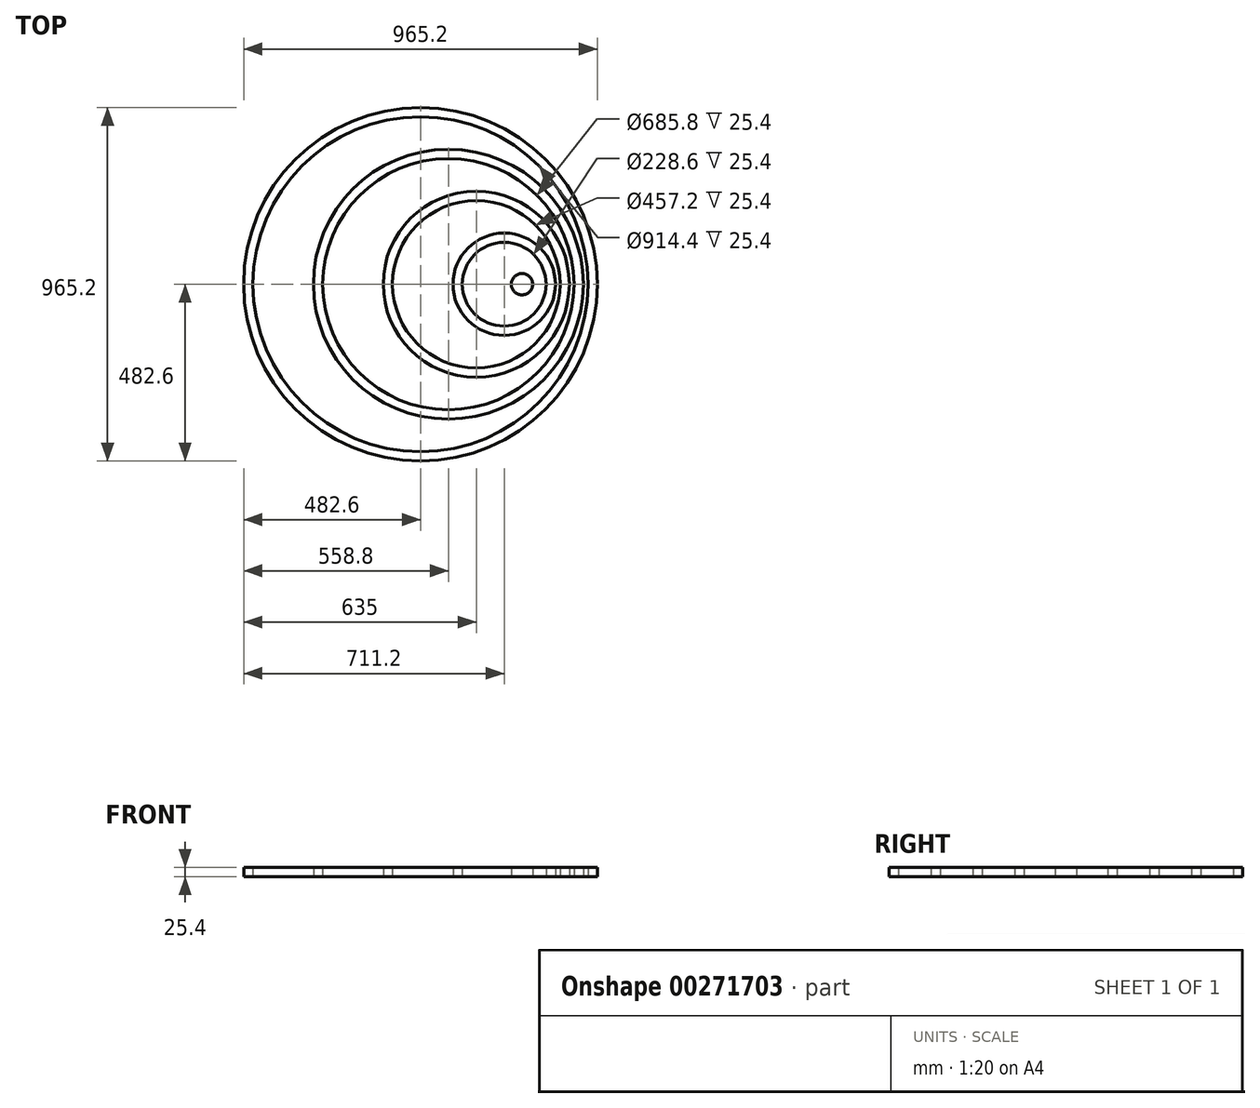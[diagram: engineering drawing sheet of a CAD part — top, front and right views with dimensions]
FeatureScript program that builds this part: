
annotation { "Feature Type Name" : "Feature", "Feature Type Description" : "" }
export const myFeature = defineFeature(function(context is Context, id is Id, definition is map)
    precondition{}
    {
        {
            var Q0;
            Q0=qCreatedBy(makeId("Top.planeOp"),FACE);
            var sketch = newSketch(context, id + "F0", { "sketchPlane" : qUnion([Q0])});
            skCircle(sketch, "E0", {"center": v(0, 0) * mm, "radius": 114.3 * mm});
            skCircle(sketch, "E1", {"center": v(-76.2, 0) * mm, "radius": 228.6 * mm});
            skCircle(sketch, "E2", {"center": v(-76.2, 0) * mm, "radius": 254 * mm});
            skCircle(sketch, "E3", {"center": v(-152.4, 0) * mm, "radius": 342.9 * mm});
            skCircle(sketch, "E4", {"center": v(-152.4, 0) * mm, "radius": 368.3 * mm});
            skCircle(sketch, "E5", {"center": v(-228.6, 0) * mm, "radius": 457.2 * mm});
            skCircle(sketch, "E6", {"center": v(-228.6, 0) * mm, "radius": 482.6 * mm});
            skCircle(sketch, "E7", {"center": v(0, 0) * mm, "radius": 139.7 * mm});
            skCircle(sketch, "E8", {"center": v(0, 0) * mm, "radius": 14.9 * mm});
            skCircle(sketch, "E9", {"center": v(48.64, 0) * mm, "radius": 29.24 * mm});
            skSolve(sketch);
        }
        {
            var Q0;
            Q0 = qSketchRegion(id + "F0", true);
            var Q1;
            Q1=makeQuery(id+"F0.imprint","IMPRINT",FACE,{"disambiguationData":[TD([[makeQuery(id+"F0.imprint","IMPRINT",EDGE,{"derivedFrom":sQuery(id+"F0.wireOp",EDGE,"E3")}),-1.0]])]});
            var Q2;
            Q2=makeQuery(id+"F0.imprint","IMPRINT",FACE,{"disambiguationData":[TD([[makeQuery(id+"F0.imprint","IMPRINT",EDGE,{"derivedFrom":sQuery(id+"F0.wireOp",EDGE,"E2")}),1.0]])]});
            extrude(context, id + "F1", {"entities" : qUnion([Q0, Q1, Q2]), "depth" : 25.4 * mm});
        }
        {
            var Q0;
            Q0=makeQuery(id+"F0.imprint","IMPRINT",FACE,{"disambiguationData":[TD([[makeQuery(id+"F0.imprint","IMPRINT",EDGE,{"derivedFrom":sQuery(id+"F0.wireOp",EDGE,"E0")}),-1.0]])]});
            extrude(context, id + "F2", {"entities" : qUnion([Q0]), "depth" : 25.4 * mm});
        }
        {
            var Q0;
            Q0 = qSketchRegion(id + "F0", true);
            extrude(context, id + "F3", {"entities" : qUnion([Q0]), "operationType" : NewBodyOperationType.ADD, "depth" : 25.4 * mm});
        }
        {
            var Q0;
            Q0=makeQuery(id+"F0.imprint","IMPRINT",FACE,{"disambiguationData":[TD([[makeQuery(id+"F0.imprint","IMPRINT",EDGE,{"derivedFrom":sQuery(id+"F0.wireOp",EDGE,"E9")}),1.0]])]});
            extrude(context, id + "F4", {"entities" : qUnion([Q0]), "depth" : 25.4 * mm});
        }
    });
